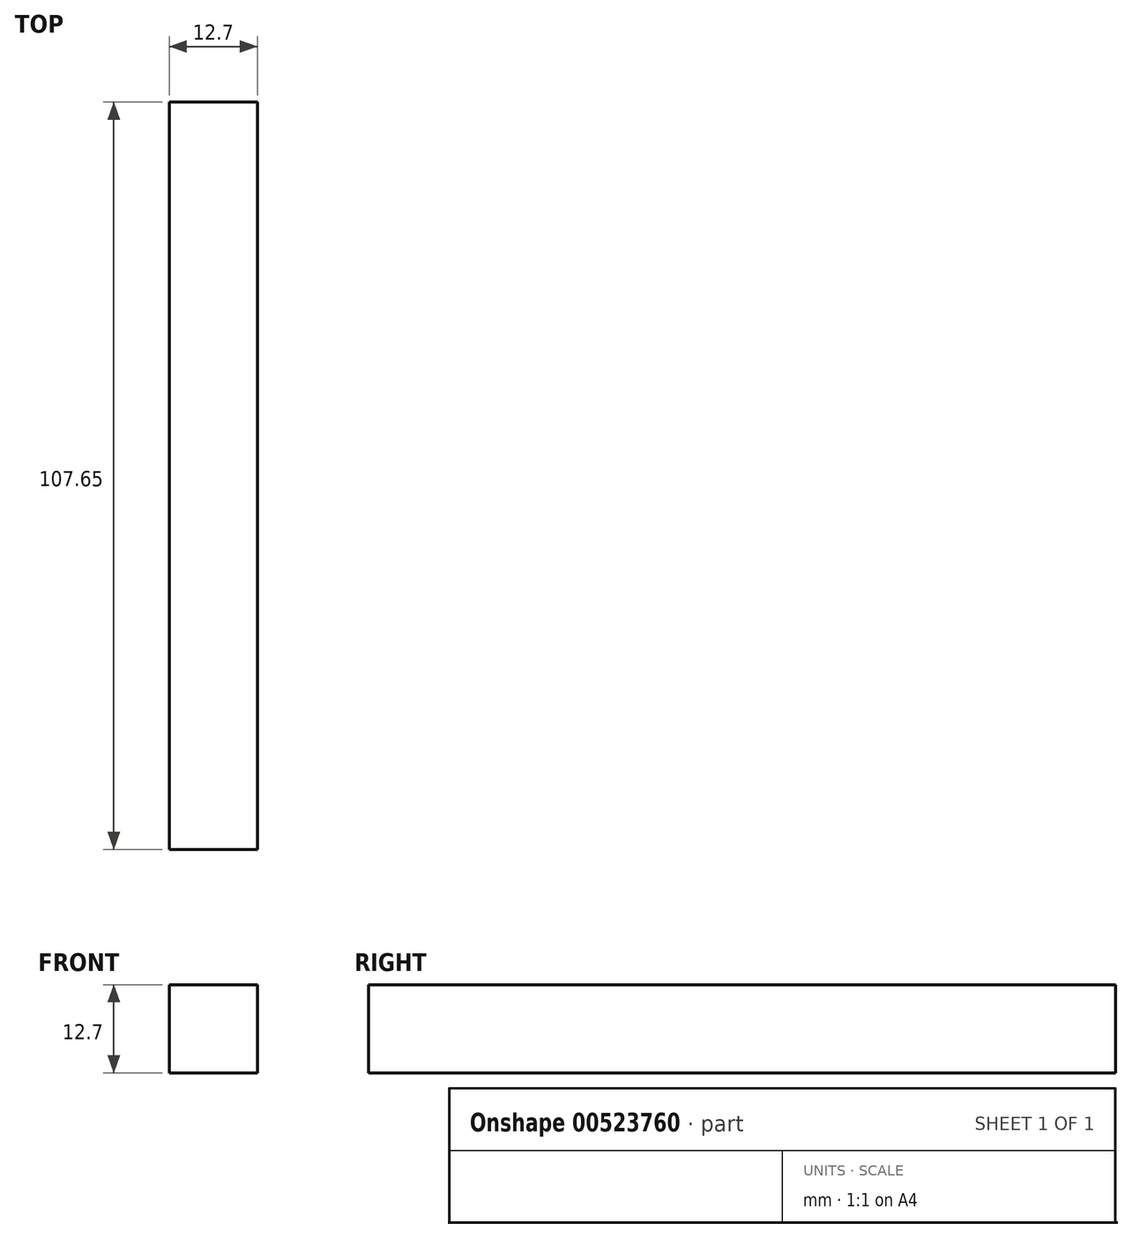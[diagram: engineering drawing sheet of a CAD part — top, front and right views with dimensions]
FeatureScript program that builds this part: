
annotation { "Feature Type Name" : "Feature", "Feature Type Description" : "" }
export const myFeature = defineFeature(function(context is Context, id is Id, definition is map)
    precondition{}
    {
        {
            var Q0;
            Q0=qCreatedBy(makeId("Front.planeOp"),FACE);
            var sketch = newSketch(context, id + "F0", { "sketchPlane" : qUnion([Q0])});
            skLineSegment(sketch, "E0", {"start": v(0, 0) * mm, "end": v(-12.7, 0) * mm});
            skLineSegment(sketch, "E1", {"start": v(-12.7, 0) * mm, "end": v(-12.7, 12.7) * mm});
            skLineSegment(sketch, "E2", {"start": v(-12.7, 12.7) * mm, "end": v(0, 12.7) * mm});
            skLineSegment(sketch, "E3", {"start": v(0, 12.7) * mm, "end": v(0, 0) * mm});
            skSolve(sketch);
        }
        {
            var Q0;
            Q0=makeQuery(id+"F0.imprint","IMPRINT",FACE,{"disambiguationData":[TD([[makeQuery(id+"F0.imprint","IMPRINT",EDGE,{"derivedFrom":sQuery(id+"F0.wireOp",EDGE,"E0")}),-1.0]])]});
            extrude(context, id + "F1", {"entities" : qUnion([Q0]), "depth" : 107.65 * mm, "offsetDistance" : 25.4 * mm});
        }
    });
